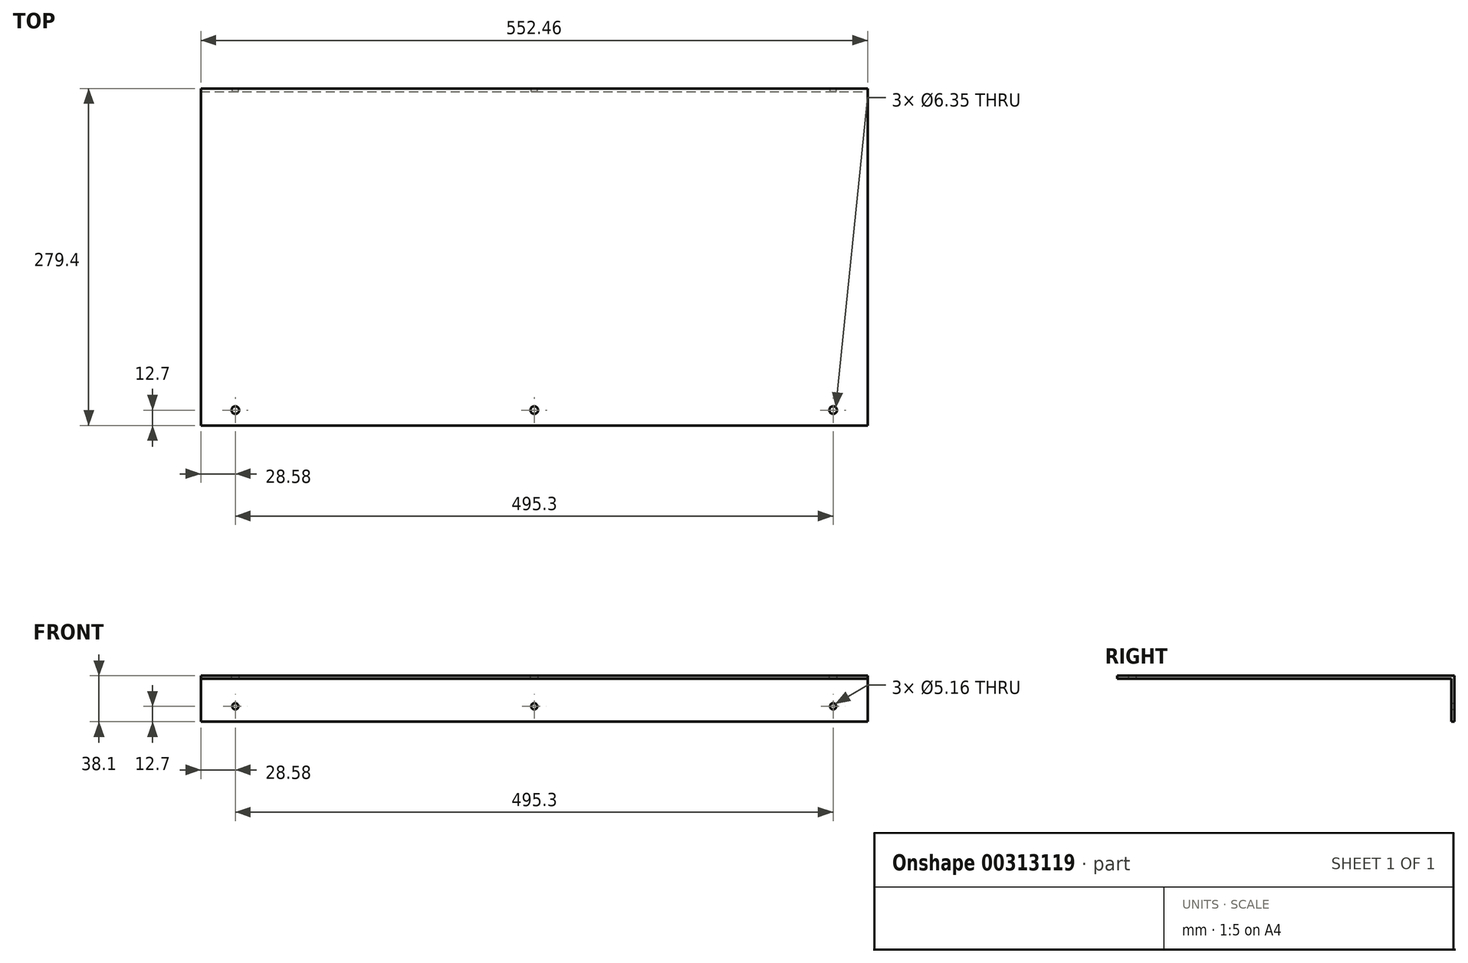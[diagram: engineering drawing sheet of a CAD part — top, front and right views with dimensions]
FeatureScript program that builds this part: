
annotation { "Feature Type Name" : "Feature", "Feature Type Description" : "" }
export const myFeature = defineFeature(function(context is Context, id is Id, definition is map)
    precondition{}
    {
        {
            var Q0;
            Q0=qCreatedBy(makeId("Top.planeOp"),FACE);
            var sketch = newSketch(context, id + "F0", { "sketchPlane" : qUnion([Q0])});
            skLineSegment(sketch, "E0.bottom", {"start": v(-276.23, -139.7) * mm, "end": v(276.23, -139.7) * mm});
            skLineSegment(sketch, "E0.top", {"start": v(-276.23, 139.7) * mm, "end": v(276.23, 139.7) * mm});
            skLineSegment(sketch, "E0.left", {"start": v(-276.23, -139.7) * mm, "end": v(-276.23, 139.7) * mm});
            skLineSegment(sketch, "E0.right", {"start": v(276.23, -139.7) * mm, "end": v(276.23, 139.7) * mm});
            skPoint(sketch, "E0.middle", {"position": v(0, 0) * mm});
            skSolve(sketch);
        }
        {
            var Q0;
            Q0 = qSketchRegion(id + "F0", true);
            extrude(context, id + "F1", {"entities" : qUnion([Q0]), "endBound" : BoundingType.SYMMETRIC, "depth" : 38.1 * mm});
        }
        {
            var Q0;
            Q0=makeQuery(id+"F1.opExtrude","SWEPT_FACE",FACE,{"disambiguationData":[OSD([sQuery(id+"F0.wireOp",EDGE,"E0.bottom")])]});
            var Q1;
            Q1=makeQuery(id+"F1.opExtrude","SWEPT_FACE",FACE,{"disambiguationData":[OSD([sQuery(id+"F0.wireOp",EDGE,"E0.left")])]});
            var Q2;
            Q2=makeQuery(id+"F1.opExtrude","CAP_FACE",FACE,{"disambiguationData":[OSD([sQuery(id+"F0.wireOp",EDGE,"E0.bottom"),sQuery(id+"F0.wireOp",EDGE,"E0.top"),sQuery(id+"F0.wireOp",EDGE,"E0.left"),sQuery(id+"F0.wireOp",EDGE,"E0.right")])],"isStart":true});
            var Q3;
            Q3=makeQuery(id+"F1.opExtrude","SWEPT_FACE",FACE,{"disambiguationData":[OSD([sQuery(id+"F0.wireOp",EDGE,"E0.right")])]});
            shell(context, id + "F2", {"entities" : qUnion([Q0, Q1, Q2, Q3]), "thickness" : 2.54 * mm});
        }
        {
            var Q0;
            Q0=makeQuery(id+"F1.opExtrude","SWEPT_FACE",FACE,{"disambiguationData":[OSD([sQuery(id+"F0.wireOp",EDGE,"E0.top")])]});
            var sketch = newSketch(context, id + "F3", { "sketchPlane" : qUnion([Q0])});
            skCircle(sketch, "E1", {"center": v(-247.65, -6.35) * mm, "radius": 2.58 * mm});
            skCircle(sketch, "E2", {"center": v(0, -6.35) * mm, "radius": 2.58 * mm});
            skPoint(sketch, "E2.centerSnap0", {"position": v(0, 19.05) * mm});
            skCircle(sketch, "E3", {"center": v(247.65, -6.35) * mm, "radius": 2.58 * mm});
            skSolve(sketch);
        }
        {
            var Q0;
            Q0 = qSketchRegion(id + "F3", true);
            var Q1;
            Q1=makeQuery(id+"F2.opShell","OFFSET_FACE",FACE,{"disambiguationData":[OSD([sQuery(id+"F0.wireOp",EDGE,"E0.top")])]});
            extrude(context, id + "F4", {"entities" : qUnion([Q0]), "operationType" : NewBodyOperationType.REMOVE, "endBound" : BoundingType.UP_TO_SURFACE, "oppositeDirection" : true, "endBoundEntityFace" : qUnion([Q1]), "depth" : 25.4 * mm});
        }
        {
            var Q0;
            Q0=makeQuery(id+"F1.opExtrude","CAP_FACE",FACE,{"disambiguationData":[OSD([sQuery(id+"F0.wireOp",EDGE,"E0.bottom"),sQuery(id+"F0.wireOp",EDGE,"E0.top"),sQuery(id+"F0.wireOp",EDGE,"E0.left"),sQuery(id+"F0.wireOp",EDGE,"E0.right")])],"isStart":false});
            var sketch = newSketch(context, id + "F5", { "sketchPlane" : qUnion([Q0])});
            skCircle(sketch, "E4", {"center": v(-247.65, -127) * mm, "radius": 3.18 * mm});
            skCircle(sketch, "E5", {"center": v(0, -127) * mm, "radius": 3.18 * mm});
            skPoint(sketch, "E5.centerSnap0", {"position": v(0, -139.7) * mm});
            skCircle(sketch, "E6", {"center": v(247.65, -127) * mm, "radius": 3.18 * mm});
            skSolve(sketch);
        }
        {
            var Q0;
            Q0 = qSketchRegion(id + "F5", true);
            extrude(context, id + "F6", {"entities" : qUnion([Q0]), "operationType" : NewBodyOperationType.REMOVE, "endBound" : BoundingType.THROUGH_ALL, "oppositeDirection" : true, "depth" : 25.4 * mm});
        }
    });
